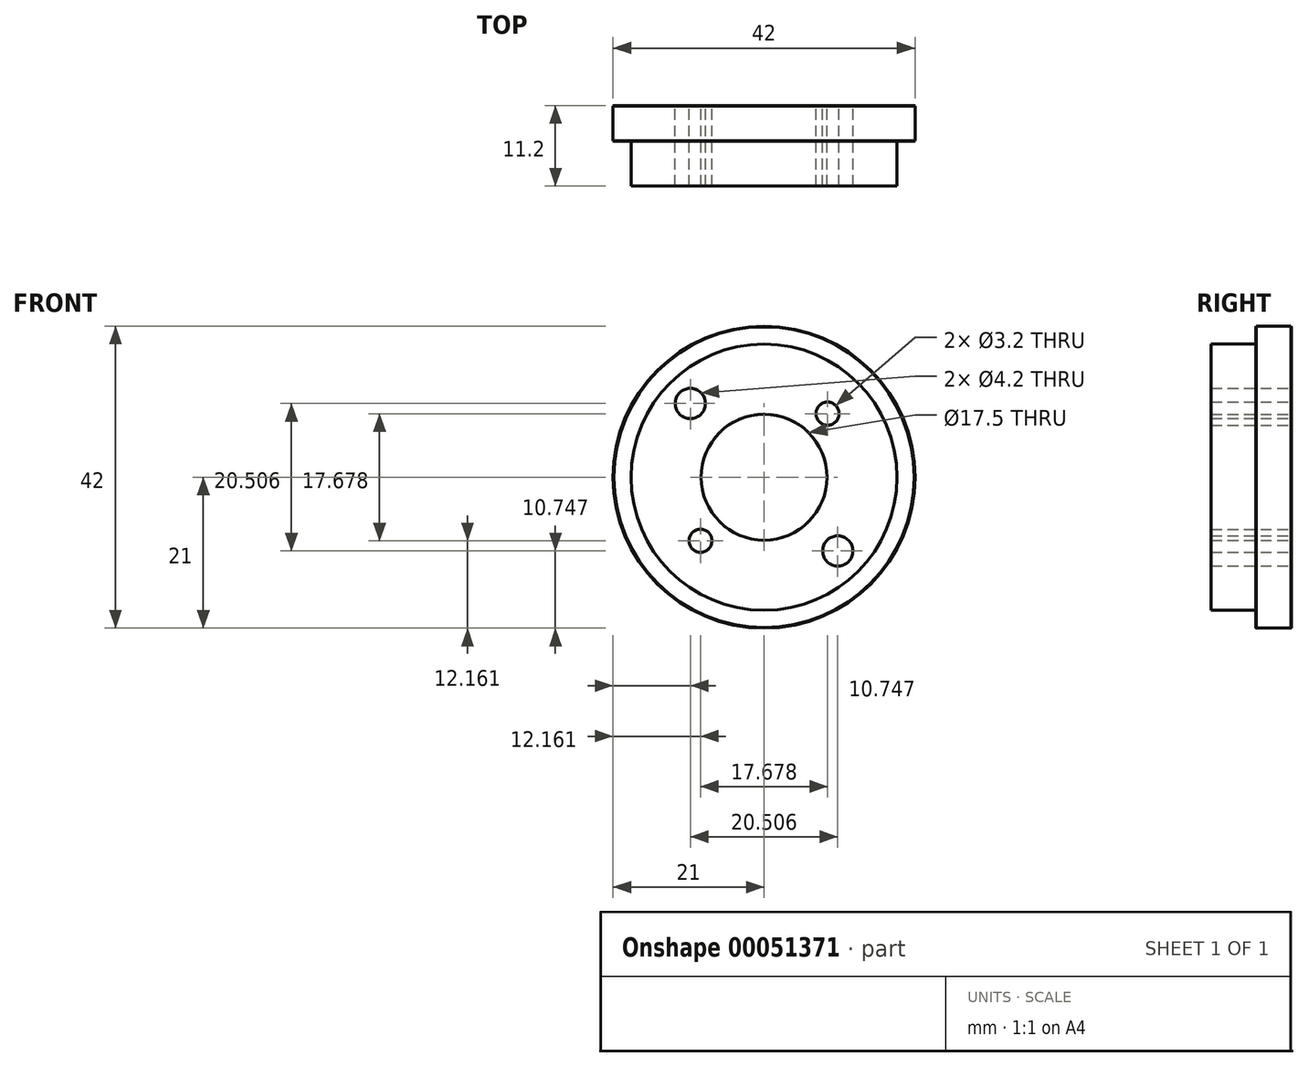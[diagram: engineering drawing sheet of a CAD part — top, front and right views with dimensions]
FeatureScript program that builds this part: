
annotation { "Feature Type Name" : "Feature", "Feature Type Description" : "" }
export const myFeature = defineFeature(function(context is Context, id is Id, definition is map)
    precondition{}
    {
        {
            var Q0;
            Q0=qCreatedBy(makeId("Front.planeOp"),FACE);
            var sketch = newSketch(context, id + "F0", { "sketchPlane" : qUnion([Q0])});
            skCircle(sketch, "E0", {"center": v(0, 0) * mm, "radius": 21 * mm});
            skSolve(sketch);
        }
        {
            var Q0;
            Q0 = qSketchRegion(id + "F0", true);
            extrude(context, id + "F1", {"entities" : qUnion([Q0]), "oppositeDirection" : true, "depth" : 5 * mm});
        }
        {
            var Q0;
            Q0=qCreatedBy(makeId("Front.planeOp"),FACE);
            var sketch = newSketch(context, id + "F2", { "sketchPlane" : qUnion([Q0])});
            skCircle(sketch, "E1", {"center": v(0, 0) * mm, "radius": 18.5 * mm});
            skSolve(sketch);
        }
        {
            var Q0;
            Q0 = qSketchRegion(id + "F2", true);
            extrude(context, id + "F3", {"entities" : qUnion([Q0]), "operationType" : NewBodyOperationType.ADD, "depth" : 6.2 * mm});
        }
        {
            var Q0;
            Q0=qCreatedBy(makeId("Front.planeOp"),FACE);
            var sketch = newSketch(context, id + "F4", { "sketchPlane" : qUnion([Q0])});
            skCircle(sketch, "E2", {"center": v(8.84, 8.84) * mm, "radius": 1.6 * mm});
            skCircle(sketch, "E3", {"center": v(-10.25, 10.25) * mm, "radius": 2.1 * mm});
            skCircle(sketch, "E4", {"center": v(-8.84, -8.84) * mm, "radius": 1.6 * mm});
            skCircle(sketch, "E5", {"center": v(10.25, -10.25) * mm, "radius": 2.1 * mm});
            skCircle(sketch, "E6", {"center": v(0, 0) * mm, "radius": 8.75 * mm});
            skLineSegment(sketch, "E7", {"start": v(-23.4, -23.4) * mm, "end": v(23.73, 23.73) * mm});
            skLineSegment(sketch, "E8", {"start": v(-25.41, 25.41) * mm, "end": v(25.28, -25.28) * mm});
            skSolve(sketch);
        }
        {
            var Q0;
            Q0 = qSketchRegion(id + "F4", true);
            extrude(context, id + "F5", {"entities" : qUnion([Q0]), "operationType" : NewBodyOperationType.REMOVE, "depth" : 6.2 * mm, "hasSecondDirection" : true, "secondDirectionOppositeDirection" : true, "secondDirectionDepth" : 5 * mm});
        }
        {
            var Q0;
            Q0=makeQuery(id+"F1.opExtrude","CAP_FACE",FACE,{"disambiguationData":[OSD([sQuery(id+"F0.wireOp",EDGE,"E0")])],"isStart":false});
            var Q1;
            Q1=makeQuery(id+"F1.opExtrude","CAP_EDGE",EDGE,{"disambiguationData":[OSD([sQuery(id+"F0.wireOp",EDGE,"E0")])],"isStart":true});
            chamfer(context, id + "F6", {"entities" : qUnion([Q0, Q1]), "width" : 0.1 * mm, "tangentPropagation" : true});
        }
    });
